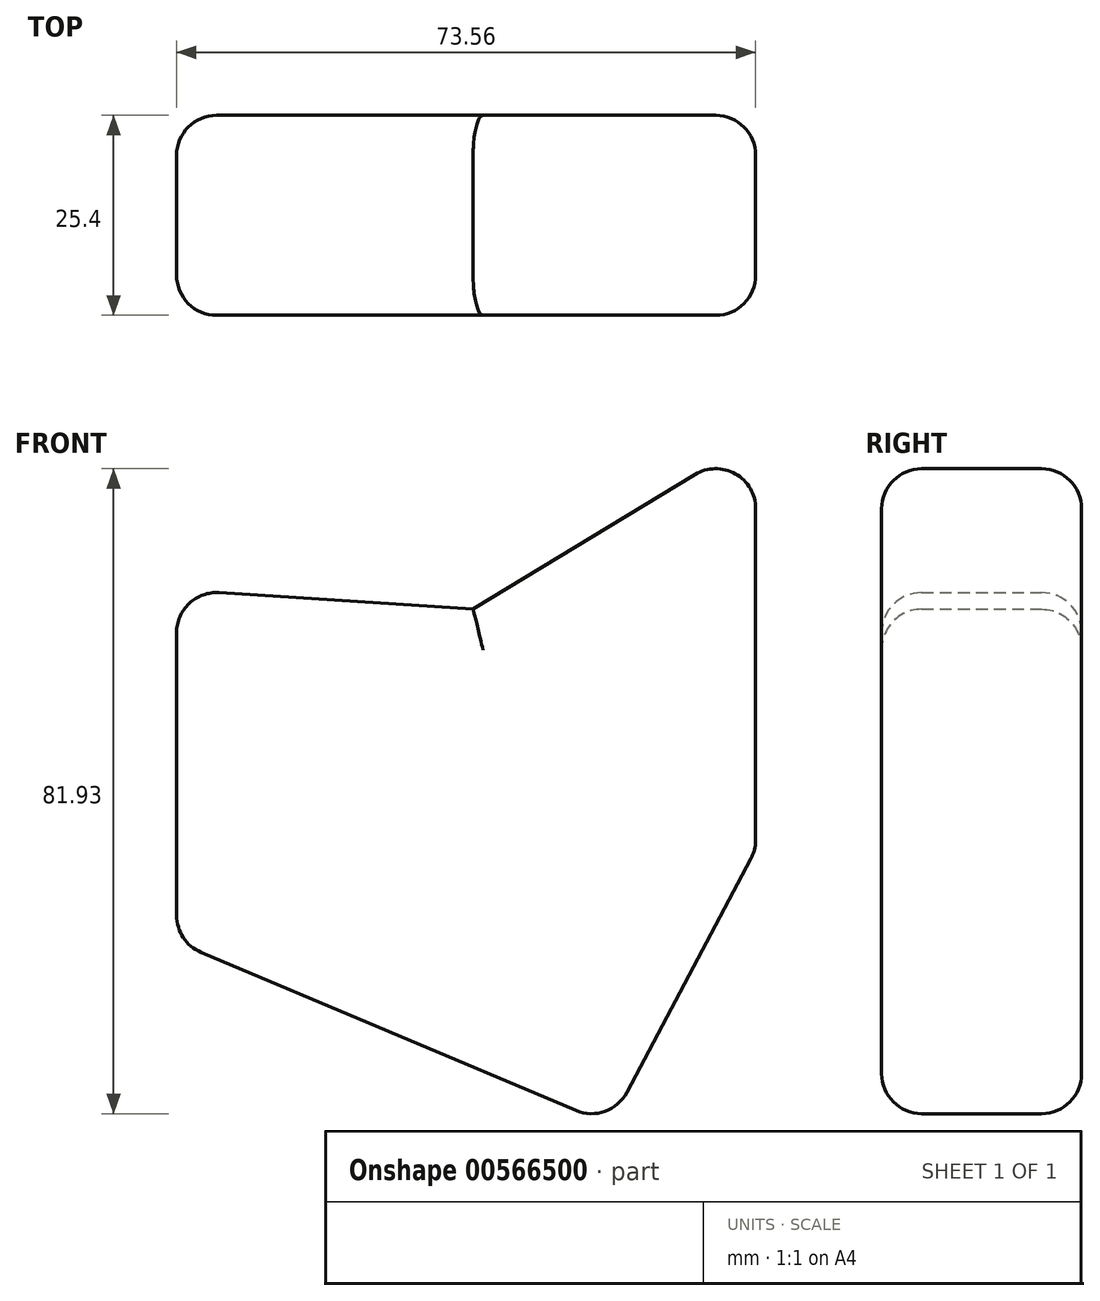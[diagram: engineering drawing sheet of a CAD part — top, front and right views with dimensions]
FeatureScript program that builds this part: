
annotation { "Feature Type Name" : "Feature", "Feature Type Description" : "" }
export const myFeature = defineFeature(function(context is Context, id is Id, definition is map)
    precondition{}
    {
        {
            var Q0;
            Q0=qCreatedBy(makeId("Front.planeOp"),FACE);
            var sketch = newSketch(context, id + "F0", { "sketchPlane" : qUnion([Q0])});
            skLineSegment(sketch, "E0", {"start": v(-40.84, 0) * mm, "end": v(-40.84, 44.73) * mm});
            skLineSegment(sketch, "E1", {"start": v(-40.84, 44.73) * mm, "end": v(-3.18, 42.28) * mm});
            skLineSegment(sketch, "E2", {"start": v(-3.18, 42.28) * mm, "end": v(32.72, 64.07) * mm});
            skLineSegment(sketch, "E3", {"start": v(32.72, 64.07) * mm, "end": v(32.72, 11.73) * mm});
            skLineSegment(sketch, "E4", {"start": v(32.72, 11.73) * mm, "end": v(14.18, -23.22) * mm});
            skLineSegment(sketch, "E5", {"start": v(-40.84, 0) * mm, "end": v(14.18, -23.22) * mm});
            skLineSegment(sketch, "E6", {"start": v(-40.84, 44.73) * mm, "end": v(-40.84, 44.73) * mm});
            skLineSegment(sketch, "E7", {"start": v(-40.84, 81.52) * mm, "end": v(-40.84, 0) * mm, "construction": true});
            skSolve(sketch);
        }
        {
            var Q0;
            Q0=makeQuery(id+"F0.imprint","IMPRINT",FACE,{"disambiguationData":[TD([[makeQuery(id+"F0.imprint","IMPRINT",EDGE,{"derivedFrom":sQuery(id+"F0.wireOp",EDGE,"E0")}),-1.0]])]});
            extrude(context, id + "F1", {"entities" : qUnion([Q0]), "depth" : 25.4 * mm, "offsetDistance" : 25.4 * mm});
        }
        {
            var Q0;
            Q0=makeQuery(id+"F1.opExtrude","CAP_EDGE",EDGE,{"disambiguationData":[OSD([sQuery(id+"F0.wireOp",EDGE,"E3")])],"isStart":false});
            var Q1;
            Q1=makeQuery(id+"F1.opExtrude","CAP_EDGE",EDGE,{"disambiguationData":[OSD([sQuery(id+"F0.wireOp",EDGE,"E3")])],"isStart":true});
            var Q2;
            Q2=makeQuery(id+"F1.opExtrude","SWEPT_EDGE",EDGE,{"disambiguationData":[OSD([sQuery(id+"F0.wireOp",EDGE,"E2"),sQuery(id+"F0.wireOp",EDGE,"E3")])]});
            var Q3;
            Q3=makeQuery(id+"F1.opExtrude","SWEPT_EDGE",EDGE,{"disambiguationData":[OSD([sQuery(id+"F0.wireOp",EDGE,"E3"),sQuery(id+"F0.wireOp",EDGE,"E4")])]});
            var Q4;
            Q4=makeQuery(id+"F1.opExtrude","SWEPT_EDGE",EDGE,{"disambiguationData":[OSD([sQuery(id+"F0.wireOp",EDGE,"E0"),sQuery(id+"F0.wireOp",EDGE,"E1")])]});
            var Q5;
            Q5=makeQuery(id+"F1.opExtrude","CAP_EDGE",EDGE,{"disambiguationData":[OSD([sQuery(id+"F0.wireOp",EDGE,"E0")])],"isStart":true});
            var Q6;
            Q6=makeQuery(id+"F1.opExtrude","CAP_EDGE",EDGE,{"disambiguationData":[OSD([sQuery(id+"F0.wireOp",EDGE,"E0")])],"isStart":false});
            var Q7;
            Q7=makeQuery(id+"F1.opExtrude","SWEPT_EDGE",EDGE,{"disambiguationData":[OSD([sQuery(id+"F0.wireOp",EDGE,"E0"),sQuery(id+"F0.wireOp",EDGE,"E5")])]});
            var Q8;
            Q8=makeQuery(id+"F1.opExtrude","CAP_EDGE",EDGE,{"disambiguationData":[OSD([sQuery(id+"F0.wireOp",EDGE,"E1")])],"isStart":true});
            var Q9;
            Q9=makeQuery(id+"F1.opExtrude","CAP_EDGE",EDGE,{"disambiguationData":[OSD([sQuery(id+"F0.wireOp",EDGE,"E2")])],"isStart":true});
            var Q10;
            Q10=makeQuery(id+"F1.opExtrude","CAP_EDGE",EDGE,{"disambiguationData":[OSD([sQuery(id+"F0.wireOp",EDGE,"E1")])],"isStart":false});
            var Q11;
            Q11=makeQuery(id+"F1.opExtrude","CAP_EDGE",EDGE,{"disambiguationData":[OSD([sQuery(id+"F0.wireOp",EDGE,"E2")])],"isStart":false});
            var Q12;
            Q12=makeQuery(id+"F1.opExtrude","CAP_EDGE",EDGE,{"disambiguationData":[OSD([sQuery(id+"F0.wireOp",EDGE,"E5")])],"isStart":false});
            var Q13;
            Q13=makeQuery(id+"F1.opExtrude","CAP_EDGE",EDGE,{"disambiguationData":[OSD([sQuery(id+"F0.wireOp",EDGE,"E5")])],"isStart":true});
            var Q14;
            Q14=makeQuery(id+"F1.opExtrude","CAP_EDGE",EDGE,{"disambiguationData":[OSD([sQuery(id+"F0.wireOp",EDGE,"E4")])],"isStart":true});
            var Q15;
            Q15=makeQuery(id+"F1.opExtrude","SWEPT_EDGE",EDGE,{"disambiguationData":[OSD([sQuery(id+"F0.wireOp",EDGE,"E4"),sQuery(id+"F0.wireOp",EDGE,"E5")])]});
            var Q16;
            Q16=makeQuery(id+"F1.opExtrude","CAP_EDGE",EDGE,{"disambiguationData":[OSD([sQuery(id+"F0.wireOp",EDGE,"E4")])],"isStart":false});
            fillet(context, id + "F2", {"entities" : qUnion([Q0, Q1, Q2, Q3, Q4, Q5, Q6, Q7, Q8, Q9, Q10, Q11, Q12, Q13, Q14, Q15, Q16]), "radius" : 5.08 * mm, "tangentPropagation" : true, "allowEdgeOverflow" : false});
        }
    });
